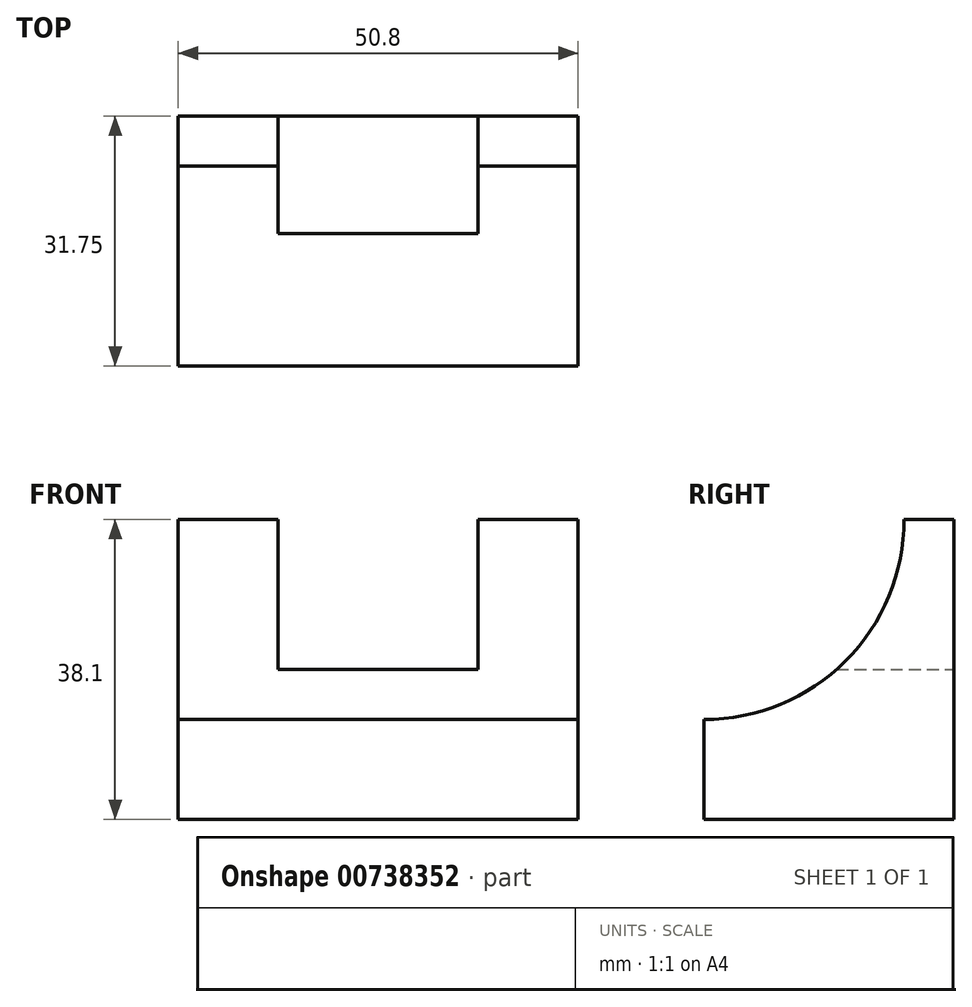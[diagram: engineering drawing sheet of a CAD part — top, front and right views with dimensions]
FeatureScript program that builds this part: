
annotation { "Feature Type Name" : "Feature", "Feature Type Description" : "" }
export const myFeature = defineFeature(function(context is Context, id is Id, definition is map)
    precondition{}
    {
        {
            var Q0;
            Q0=qCreatedBy(makeId("Front.planeOp"),FACE);
            var sketch = newSketch(context, id + "F0", { "sketchPlane" : qUnion([Q0])});
            skLineSegment(sketch, "E0", {"start": v(0, 0) * mm, "end": v(50.8, 0) * mm});
            skLineSegment(sketch, "E1", {"start": v(50.8, 0) * mm, "end": v(50.8, 38.1) * mm});
            skLineSegment(sketch, "E2", {"start": v(50.8, 38.1) * mm, "end": v(0, 38.1) * mm});
            skLineSegment(sketch, "E3", {"start": v(0, 38.1) * mm, "end": v(0, 0) * mm});
            skSolve(sketch);
        }
        {
            var Q0;
            Q0 = qSketchRegion(id + "F0", true);
            extrude(context, id + "F1", {"entities" : qUnion([Q0]), "depth" : 31.75 * mm, "offsetDistance" : 25.4 * mm});
        }
        {
            var Q0;
            Q0=makeQuery(id+"F1.opExtrude","SWEPT_FACE",FACE,{"disambiguationData":[OSD([sQuery(id+"F0.wireOp",EDGE,"E1")])]});
            var sketch = newSketch(context, id + "F2", { "sketchPlane" : qUnion([Q0])});
            skLineSegment(sketch, "E4", {"start": v(-31.75, 0) * mm, "end": v(-31.75, 12.7) * mm});
            skArc(sketch, "E5", {"start": v(-31.75, 12.7) * mm, "mid": v(-13.78, 20.13) * mm, "end": v(-6.35, 38.1) * mm});
            skSolve(sketch);
        }
        {
            var Q0;
            Q0 = qSketchRegion(id + "F2", true);
            var Q1;
            {var subQ0=sQuery(id+"F2.wireOp",EDGE,"E5");Q1=makeQuery(id+"F2.imprint","IMPRINT",FACE,{"disambiguationData":[TD([[makeQuery(id+"F2.imprint","IMPRINT",EDGE,{"derivedFrom":subQ0}),1.0]])]});}
            extrude(context, id + "F3", {"entities" : qUnion([Q0, Q1]), "operationType" : NewBodyOperationType.REMOVE, "endBound" : BoundingType.THROUGH_ALL, "oppositeDirection" : true, "depth" : 25.4 * mm, "offsetDistance" : 25.4 * mm});
        }
        {
            var Q0;
            Q0=makeQuery(id+"F1.opExtrude","CAP_FACE",FACE,{"disambiguationData":[OSD([sQuery(id+"F0.wireOp",EDGE,"E0"),sQuery(id+"F0.wireOp",EDGE,"E1"),sQuery(id+"F0.wireOp",EDGE,"E2"),sQuery(id+"F0.wireOp",EDGE,"E3")])],"isStart":true});
            var sketch = newSketch(context, id + "F4", { "sketchPlane" : qUnion([Q0])});
            skLineSegment(sketch, "E6", {"start": v(-50.8, 38.1) * mm, "end": v(-38.1, 38.1) * mm});
            skLineSegment(sketch, "E7", {"start": v(-38.1, 38.1) * mm, "end": v(-38.1, 19.05) * mm});
            skLineSegment(sketch, "E8", {"start": v(-38.1, 19.05) * mm, "end": v(-12.7, 19.05) * mm});
            skLineSegment(sketch, "E9", {"start": v(-12.7, 19.05) * mm, "end": v(-12.7, 38.1) * mm});
            skLineSegment(sketch, "E10", {"start": v(-12.7, 38.1) * mm, "end": v(0, 38.1) * mm});
            skSolve(sketch);
        }
        {
            var Q0;
            Q0 = qSketchRegion(id + "F4", true);
            var Q1;
            {var subQ0=sQuery(id+"F4.wireOp",EDGE,"E7");Q1=makeQuery(id+"F4.imprint","IMPRINT",FACE,{"disambiguationData":[TD([[makeQuery(id+"F4.imprint","IMPRINT",EDGE,{"derivedFrom":subQ0}),1.0]])]});}
            extrude(context, id + "F5", {"entities" : qUnion([Q0, Q1]), "operationType" : NewBodyOperationType.REMOVE, "endBound" : BoundingType.THROUGH_ALL, "oppositeDirection" : true, "depth" : 25.4 * mm, "offsetDistance" : 25.4 * mm});
        }
    });
